# Revit family: Bike_Rack-Saris_Parking-Stretch_Rack
name_source: partatom
category: Site
revit_build: Autodesk Revit 2014 (Build: 20140709_2115(x64)
units: mm (PartAtom-declared; Revit-internal decimal feet)

## types (8) — shared parameters
Assembly Code = G2040500
Ceiling Clearance = 96 Inches Ceiling Clearance Required
Default Elevation = 48 "
Description = High density long term bike storage
Manufacturer = Saris Parking
Mount Color = Paint - Saris Parking - Powder Coat - Shuttle Black
Product Documentation Link = https://www.sarisparking.com
Product Page URL = https://www.sarisparking.com
URL = https://www.sarisparking.com

## per-type parameters (varying)
| type | 8010 | 8016 | 8018 | 8080 | Model | Stretch Rack Locking | Width |
| 10-Bike Locking | Yes | No | No | No | 8110 | Yes | 72.4 " |
| 8-Bike 72" Locking | No | No | No | Yes | 8180 | Yes | 72.4 " |
| 6-Bike Locking | No | Yes | No | No | 8116 | Yes | 54.4 " |
| 8-Bike 54" Locking | No | No | Yes | No | 8118 | Yes | 54.4 " |
| 10-Bike | Yes | No | No | No | 8010 | No | 72.4 " |
| 8-Bike 72" | No | No | No | Yes | 8080 | No | 72.4 " |
| 6-Bike | No | Yes | No | No | 8016 | No | 54.4 " |
| 8-Bike 54" | No | No | Yes | No | 8018 | No | 54.4 " |

## geometry (parser evidence)
native form markers: Sweep x27
no freeform markers — native parametric forms only
